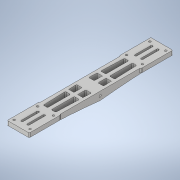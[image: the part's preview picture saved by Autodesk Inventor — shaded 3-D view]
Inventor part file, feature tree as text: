
AUTODESK INVENTOR PART (.ipt)
format: ipt  version: 2020 (Build 240168000, 168)  size: 601,088 bytes
history: native  units: in
note: dims shown in document units (in); Inventor stores cm internally (conversion verified against a paired STEP export)
features: extrude x16, sketch x15, fillet x4, plane x2, mirror x2, pattern_linear x1
ambient origin geometry x8: Origin, YZ Plane, XZ Plane, XY Plane, X Axis, Y Axis, Z Axis, Center Point
bodies: Solid1 (feature_tree)
feature tree (40):
  extrude  "Extrusion1"  Depth=4.5in
  fillet  "Fillet1"  Radius=4.5in
  extrude  "Extrusion2"  Depth=0.25in
  extrude  "Extrusion3"  Depth=0.625in
  extrude  "Extrusion4"  Depth=1.25in
  extrude  "Extrusion5"  Depth=0.8125in TaperAngle=0.0deg
  plane  "Work Plane1"
  extrude  "Extrusion6"  Depth=9.0in
  extrude  "Extrusion7"  Depth=0.625in
  fillet  "Fillet6"  Radius=6.0in
  extrude  "Extrusion9"  Depth=1.25in
  extrude  "Extrusion11"  Depth=0.125in
  extrude  "Extrusion10"  Depth=0.748in
  extrude  "Extrusion13"  Depth=0.748in
  extrude  "Extrusion14"  Depth=0.125in
  extrude  "Extrusion15"  Depth=0.125in
  extrude  "Extrusion16"  Depth=0.125in
  pattern_linear  "Rectangular Pattern2"  Spacing1=0.125in  [1 undecoded]
  extrude  "Extrusion17"  Depth=0.055in
  extrude  "Extrusion18"  Depth=0.25in
  plane  "Work Plane2"
  mirror  "Mirror4"
  fillet  "Fillet7"  Radius=0.25in
  fillet  "Fillet8"  Radius=1.0in
  mirror  "Mirror5"
  sketch  "Sketch1"  dims[d0=0.5in d1=4.5in d2=4.5in]
  sketch  "Sketch2"  dims[d3=0.25in d4=0.135in]
  sketch  "Sketch3"  dims[d5=1.25in d6=0.0in d7=0.625in]
  sketch  "Sketch4"  dims[d8=4.5in d9=1.25in]
  sketch  "Sketch5"  dims[d10=0.5in d13=0.8125in d14=0.0in]
  sketch  "Sketch9"  dims[d15=1.25in d16=9.0in]
  sketch  "Sketch11"  dims[d17=1.0in d18=0.0in d19=0.625in d20=6.0in]
  sketch  "Sketch12"  dims[d21=6.0in d22=1.25in]
  sketch  "Sketch14"  dims[d23=1.5in d26=0.125in]
  sketch  "Sketch16"  dims[d27=1.0in d28=0.0in d30=0.748in]
  sketch  "Sketch17"  dims[d31=0.6299in d32=0.748in]
  sketch  "Sketch19"  dims[d33=0.6299in d34=0.125in]
  sketch  "Sketch20"  dims[d35=0.125in d36=0.125in]
  sketch  "Sketch21"  dims[d37=0.125in d38=0.125in]
  sketch  "Sketch22"  dims[d39=0.125in d40=0.125in d41=0.125in d42=0.25in d43=0.25in d44=1.0in d45=0.0in d46=-0.1969in d47=0.2362in d48=0.2362in d49=0.2362in d50=0.2362in d51=0.2362in d52=0.2362in d53=0.2362in d54=0.2362in d55=1.0in d56=0.0in d60=0.3435in d61=0.9162in d62=2.8in d63=0.225in d64=1.0in d65=0.0in d70=0.125in d71=2.65in d72=0.25in d73=0.0in d74=0.8in d75=0.5in d76=0.0in d77=0.45in d78=0.254in d79=0.0in d82=0.254in d83=0.0in d84=0.136in d85=0.144in d86=0.125in d87=0.54in d88=0.0in d92=0.5in d93=0.542in d94=1.084in d95=1.0in d96=0.54in d97=0.0in d98=0.125in d99=3.1496in d101=0.125in d102=0.3937in d104=1.0in d106=0.24in d107=0.0in d108=0.5in d109=0.462in d110=0.7874in d112=1.438in d113=0.1in d114=0.0in d115=0.05in d116=0.0in d117=0.055in d118=0.625in d119=0.055in d80=0.5in d81=0.0344in d111=0.0344in]
note: 1 required parameter value undecoded (feature->parameter linkage not recoverable at this tier; creation-order binding heuristic only, values carry confidence <= 0.55)
